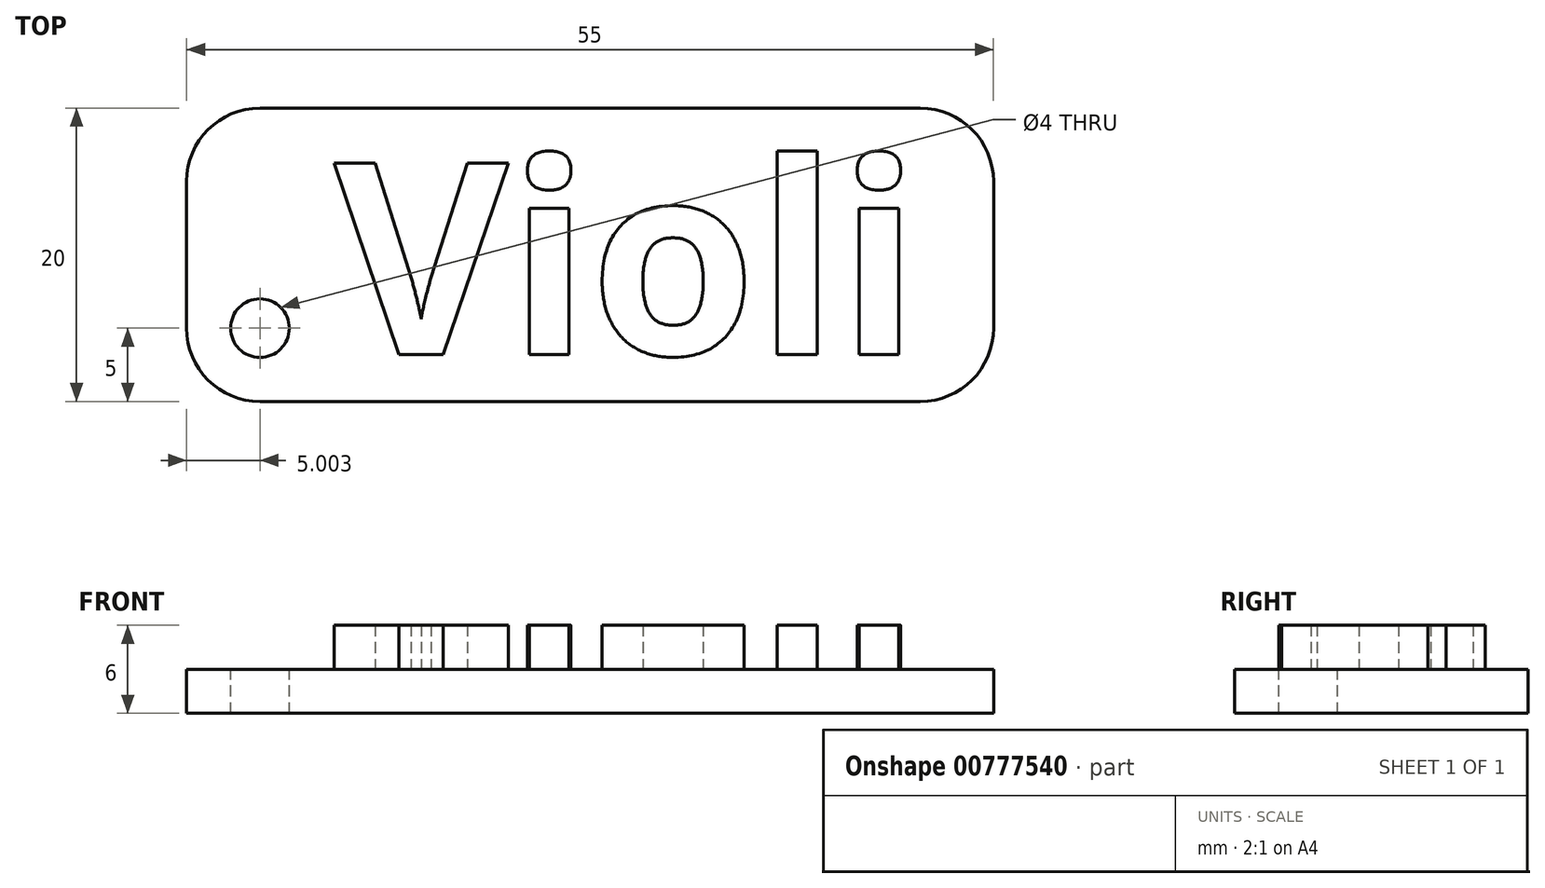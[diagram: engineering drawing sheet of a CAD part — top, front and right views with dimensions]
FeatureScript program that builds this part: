
annotation { "Feature Type Name" : "Feature", "Feature Type Description" : "" }
export const myFeature = defineFeature(function(context is Context, id is Id, definition is map)
    precondition{}
    {
        {
            var Q0;
            Q0=qCreatedBy(makeId("Top.planeOp"),FACE);
            var sketch = newSketch(context, id + "F0", { "sketchPlane" : qUnion([Q0])});
            skLineSegment(sketch, "E0.bottom", {"start": v(-43.23, 7.11) * mm, "end": v(11.77, 7.11) * mm});
            skLineSegment(sketch, "E0.top", {"start": v(-43.23, -12.89) * mm, "end": v(11.77, -12.89) * mm});
            skLineSegment(sketch, "E0.left", {"start": v(-43.23, 7.11) * mm, "end": v(-43.23, -12.89) * mm});
            skLineSegment(sketch, "E0.right", {"start": v(11.77, 7.11) * mm, "end": v(11.77, -12.89) * mm});
            skSolve(sketch);
        }
        {
            var Q0;
            Q0 = qSketchRegion(id + "F0", true);
            extrude(context, id + "F1", {"entities" : qUnion([Q0]), "depth" : 3 * mm, "offsetDistance" : 25 * mm});
        }
        {
            var Q0;
            Q0=makeQuery(id+"F1.opExtrude","CAP_FACE",FACE,{"disambiguationData":[OSD([sQuery(id+"F0.wireOp",EDGE,"E0.bottom"),sQuery(id+"F0.wireOp",EDGE,"E0.top"),sQuery(id+"F0.wireOp",EDGE,"E0.left"),sQuery(id+"F0.wireOp",EDGE,"E0.right")])],"isStart":false});
            var sketch = newSketch(context, id + "F2", { "sketchPlane" : qUnion([Q0])});
            skText(sketch, "E1", { "text": "Violi", "fontName": "OpenSans-Bold.ttf"});
            const initialGuessF2  = {"E1": [-0.03318, -0.0097, 1, 0, 0.01316]};
            skSetInitialGuess(sketch, initialGuessF2);
            skSolve(sketch);
        }
        {
            var Q0;
            Q0 = qSketchRegion(id + "F2", true);
            extrude(context, id + "F3", {"entities" : qUnion([Q0]), "operationType" : NewBodyOperationType.ADD, "depth" : 3 * mm, "offsetDistance" : 25 * mm});
        }
        {
            var Q0;
            Q0=makeQuery(id+"F1.opExtrude","SWEPT_EDGE",EDGE,{"disambiguationData":[OSD([sQuery(id+"F0.wireOp",EDGE,"E0.bottom"),sQuery(id+"F0.wireOp",EDGE,"E0.left")])]});
            var Q1;
            Q1=makeQuery(id+"F1.opExtrude","SWEPT_EDGE",EDGE,{"disambiguationData":[OSD([sQuery(id+"F0.wireOp",EDGE,"E0.top"),sQuery(id+"F0.wireOp",EDGE,"E0.left")])]});
            var Q2;
            Q2=makeQuery(id+"F1.opExtrude","SWEPT_EDGE",EDGE,{"disambiguationData":[OSD([sQuery(id+"F0.wireOp",EDGE,"E0.top"),sQuery(id+"F0.wireOp",EDGE,"E0.right")])]});
            var Q3;
            Q3=makeQuery(id+"F1.opExtrude","SWEPT_EDGE",EDGE,{"disambiguationData":[OSD([sQuery(id+"F0.wireOp",EDGE,"E0.bottom"),sQuery(id+"F0.wireOp",EDGE,"E0.right")])]});
            fillet(context, id + "F4", {"entities" : qUnion([Q0, Q1, Q2, Q3]), "radius" : 5 * mm, "tangentPropagation" : true, "allowEdgeOverflow" : false});
        }
        {
            var Q0;
            {var subQ0=sQuery(id+"F0.wireOp",EDGE,"E0.top");var subQ1=sQuery(id+"F0.wireOp",EDGE,"E0.right");var subQ2=sQuery(id+"F0.wireOp",EDGE,"E0.bottom");var subQ3=sQuery(id+"F0.wireOp",EDGE,"E0.left");Q0=makeQuery(id+"F3.boolean.opBoolean","SPLIT",FACE,{"disambiguationData":[TD([makeQuery(id+"F1.opExtrude","SWEPT_FACE",FACE,{"disambiguationData":[OSD([subQ2])]})])],"derivedFrom":makeQuery(id+"F1.opExtrude","CAP_FACE",FACE,{"disambiguationData":[OSD([subQ2,subQ0,subQ3,subQ1])],"isStart":false})});}
            var sketch = newSketch(context, id + "F5", { "sketchPlane" : qUnion([Q0])});
            skCircle(sketch, "E2", {"center": v(-38.23, -7.89) * mm, "radius": 2 * mm});
            skSolve(sketch);
        }
        {
            var Q0;
            Q0 = qSketchRegion(id + "F5", true);
            extrude(context, id + "F6", {"entities" : qUnion([Q0]), "operationType" : NewBodyOperationType.REMOVE, "oppositeDirection" : true, "depth" : 25 * mm, "offsetDistance" : 25 * mm});
        }
    });
